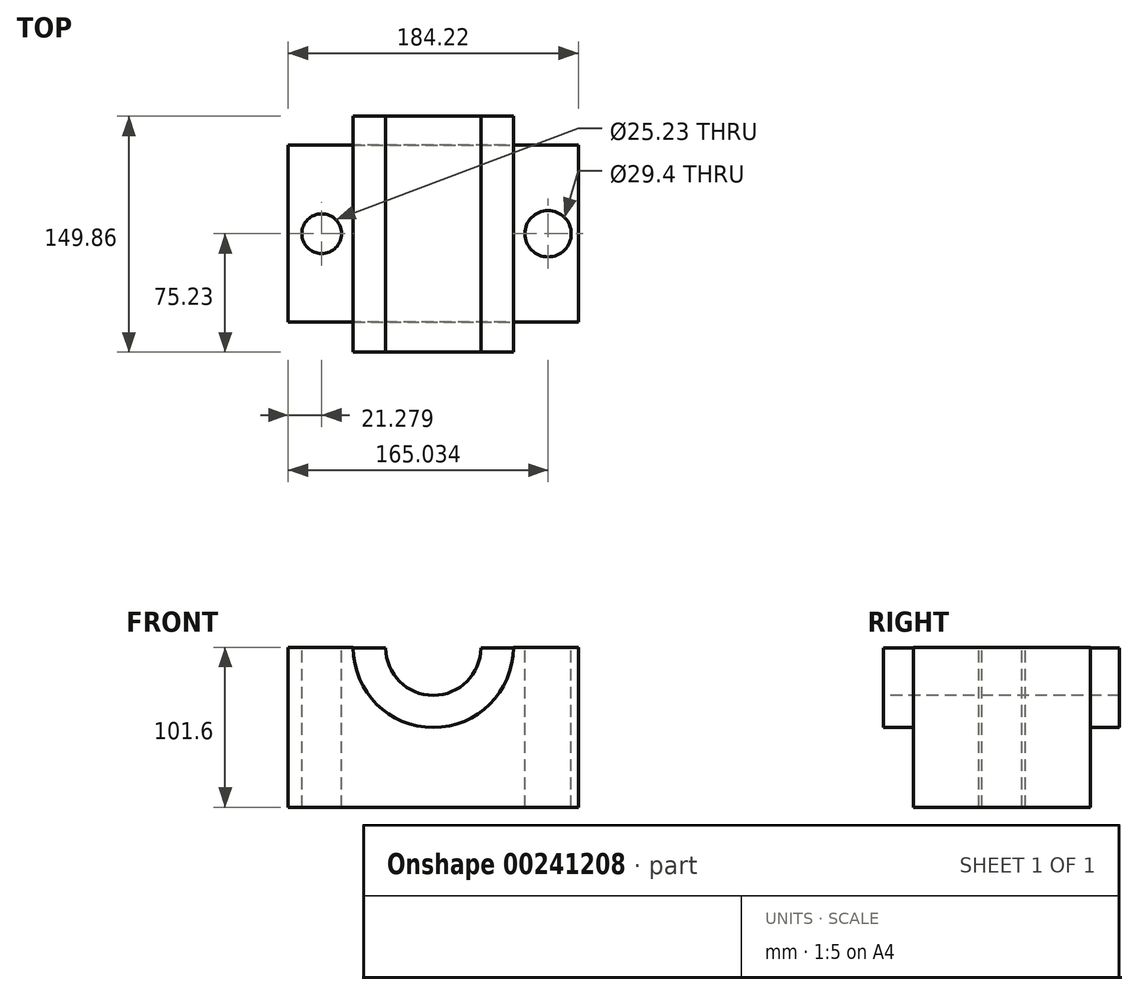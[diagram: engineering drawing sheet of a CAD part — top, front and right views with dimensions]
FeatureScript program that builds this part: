
annotation { "Feature Type Name" : "Feature", "Feature Type Description" : "" }
export const myFeature = defineFeature(function(context is Context, id is Id, definition is map)
    precondition{}
    {
        {
            var Q0;
            Q0=qCreatedBy(makeId("Top.planeOp"),FACE);
            var sketch = newSketch(context, id + "F0", { "sketchPlane" : qUnion([Q0])});
            skLineSegment(sketch, "E0.bottom", {"start": v(92.1, 56.18) * mm, "end": v(-92.1, 56.18) * mm});
            skLineSegment(sketch, "E0.top", {"start": v(92.1, -56.18) * mm, "end": v(-92.1, -56.18) * mm});
            skLineSegment(sketch, "E0.left", {"start": v(92.1, 56.18) * mm, "end": v(92.1, -56.18) * mm});
            skLineSegment(sketch, "E0.right", {"start": v(-92.1, 56.18) * mm, "end": v(-92.1, -56.18) * mm});
            skPoint(sketch, "E0.middle", {"position": v(0, 0) * mm});
            skSolve(sketch);
        }
        {
            var Q0;
            Q0 = qSketchRegion(id + "F0", true);
            extrude(context, id + "F1", {"entities" : qUnion([Q0]), "depth" : 101.6 * mm});
        }
        {
            var Q0;
            Q0=makeQuery(id+"F1.opExtrude","SWEPT_FACE",FACE,{"disambiguationData":[OSD([sQuery(id+"F0.wireOp",EDGE,"E0.top")])]});
            var sketch = newSketch(context, id + "F2", { "sketchPlane" : qUnion([Q0])});
            skCircle(sketch, "E1", {"center": v(0, 101.6) * mm, "radius": 50.92 * mm});
            skSolve(sketch);
        }
        {
            var Q0;
            Q0 = qSketchRegion(id + "F2", true);
            extrude(context, id + "F3", {"entities" : qUnion([Q0]), "operationType" : NewBodyOperationType.ADD, "depth" : 19.05 * mm});
        }
        {
            var Q0;
            Q0=makeQuery(id+"F3.opExtrude","CAP_FACE",FACE,{"disambiguationData":[OSD([sQuery(id+"F2.wireOp",EDGE,"E1")])],"isStart":false});
            extrude(context, id + "F4", {"entities" : qUnion([Q0]), "operationType" : NewBodyOperationType.ADD, "oppositeDirection" : true, "depth" : 149.86 * mm});
        }
        {
            var Q0;
            Q0=makeQuery(id+"F3.opExtrude","CAP_FACE",FACE,{"disambiguationData":[OSD([sQuery(id+"F2.wireOp",EDGE,"E1")])],"isStart":false});
            var sketch = newSketch(context, id + "F5", { "sketchPlane" : qUnion([Q0])});
            skArc(sketch, "E2", {"start": v(50.92, 101.24) * mm, "mid": v(0, 152.98) * mm, "end": v(-50.92, 101.24) * mm});
            skLineSegment(sketch, "E3", {"start": v(-50.92, 101.24) * mm, "end": v(50.92, 101.24) * mm});
            skSolve(sketch);
        }
        {
            var Q0;
            {var subQ0=sQuery(id+"F5.wireOp",EDGE,"E3");Q0=makeQuery(id+"F5.imprint","IMPRINT",FACE,{"disambiguationData":[TD([[makeQuery(id+"F5.imprint","IMPRINT",EDGE,{"derivedFrom":subQ0}),1.0]])]});}
            extrude(context, id + "F6", {"entities" : qUnion([Q0]), "operationType" : NewBodyOperationType.REMOVE, "oppositeDirection" : true, "depth" : 330.2 * mm});
        }
        {
            var Q0;
            {var subQ0=sQuery(id+"F0.wireOp",EDGE,"E0.right");var subQ2=sQuery(id+"F0.wireOp",EDGE,"E0.top");var subQ3=sQuery(id+"F0.wireOp",EDGE,"E0.bottom");Q0=makeQuery(id+"F4.boolean.opBoolean","SPLIT",FACE,{"disambiguationData":[TD([makeQuery(id+"F1.opExtrude","SWEPT_FACE",FACE,{"disambiguationData":[OSD([subQ0])]})])],"derivedFrom":makeQuery(id+"F1.opExtrude","CAP_FACE",FACE,{"disambiguationData":[OSD([subQ3,subQ2,sQuery(id+"F0.wireOp",EDGE,"E0.left"),subQ0])],"isStart":false})});}
            var sketch = newSketch(context, id + "F7", { "sketchPlane" : qUnion([Q0])});
            skCircle(sketch, "E4", {"center": v(-70.83, 0) * mm, "radius": 12.62 * mm});
            skCircle(sketch, "E5", {"center": v(72.92, 0) * mm, "radius": 14.7 * mm});
            skSolve(sketch);
        }
        {
            var Q0;
            Q0 = qSketchRegion(id + "F7", true);
            extrude(context, id + "F8", {"entities" : qUnion([Q0]), "operationType" : NewBodyOperationType.REMOVE, "oppositeDirection" : true, "depth" : 254 * mm});
        }
        {
            var Q0;
            Q0=makeQuery(id+"F3.opExtrude","CAP_FACE",FACE,{"disambiguationData":[OSD([sQuery(id+"F2.wireOp",EDGE,"E1")])],"isStart":false});
            var sketch = newSketch(context, id + "F9", { "sketchPlane" : qUnion([Q0])});
            skCircle(sketch, "E6", {"center": v(0, 101.24) * mm, "radius": 30.18 * mm});
            skSolve(sketch);
        }
        {
            var Q0;
            Q0 = qSketchRegion(id + "F9", true);
            extrude(context, id + "F10", {"entities" : qUnion([Q0]), "operationType" : NewBodyOperationType.REMOVE, "oppositeDirection" : true, "depth" : 381 * mm});
        }
    });
